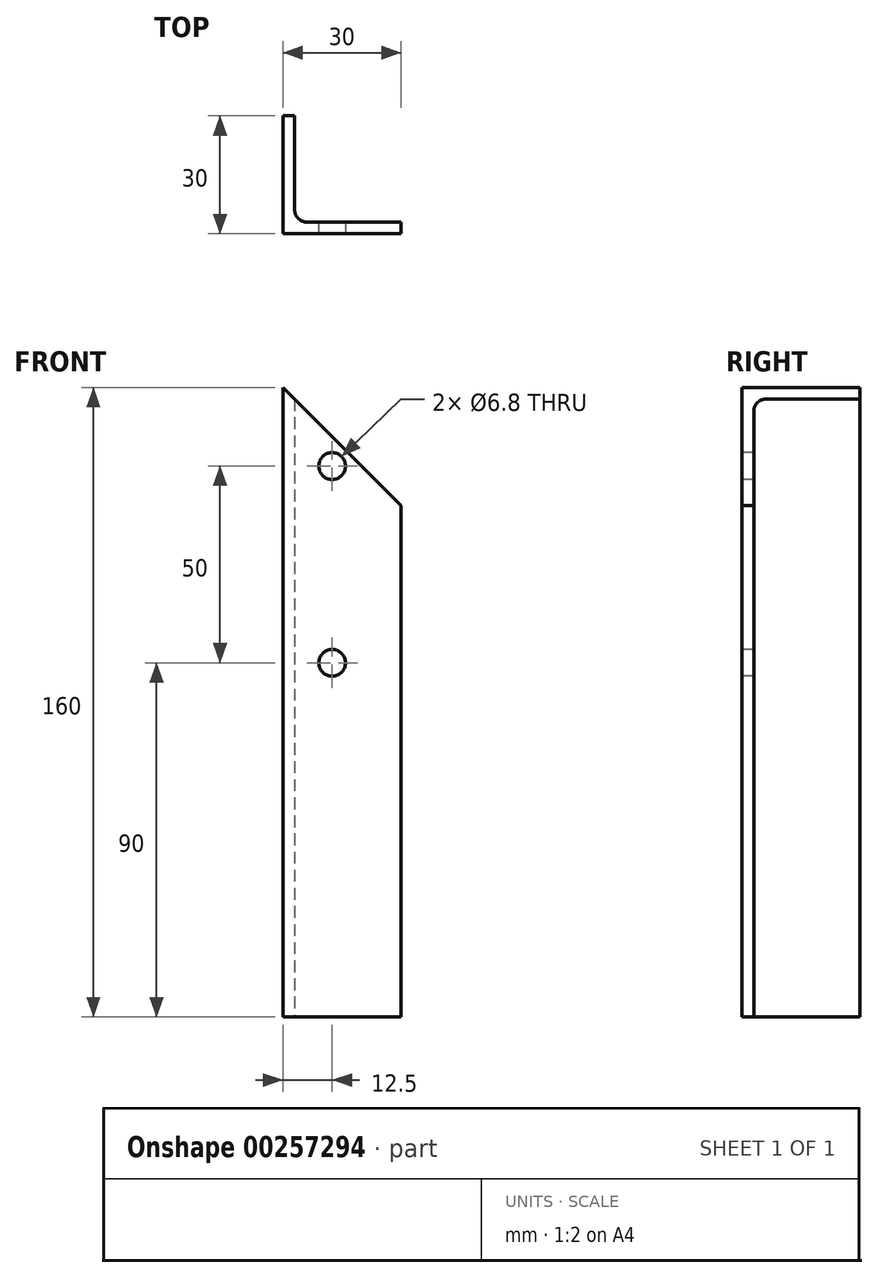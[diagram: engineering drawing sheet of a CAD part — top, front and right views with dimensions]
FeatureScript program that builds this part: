
annotation { "Feature Type Name" : "Feature", "Feature Type Description" : "" }
export const myFeature = defineFeature(function(context is Context, id is Id, definition is map)
    precondition{}
    {
        {
            var Q0;
            Q0=qCreatedBy(makeId("Top.planeOp"),FACE);
            var sketch = newSketch(context, id + "F0", { "sketchPlane" : qUnion([Q0])});
            skLineSegment(sketch, "E0", {"start": v(0, 30) * mm, "end": v(0, 0) * mm});
            skLineSegment(sketch, "E1", {"start": v(0, 0) * mm, "end": v(30, 0) * mm});
            skLineSegment(sketch, "E2", {"start": v(30, 0) * mm, "end": v(30, 3) * mm});
            skLineSegment(sketch, "E3", {"start": v(30, 3) * mm, "end": v(3, 3) * mm});
            skLineSegment(sketch, "E4", {"start": v(3, 3) * mm, "end": v(3, 30) * mm});
            skLineSegment(sketch, "E5", {"start": v(3, 30) * mm, "end": v(0, 30) * mm});
            skSolve(sketch);
        }
        {
            var Q0;
            Q0=makeQuery(id+"F0.imprint","IMPRINT",FACE,{"disambiguationData":[TD([[makeQuery(id+"F0.imprint","IMPRINT",EDGE,{"derivedFrom":sQuery(id+"F0.wireOp",EDGE,"E0")}),1.0]])]});
            extrude(context, id + "F1", {"entities" : qUnion([Q0]), "depth" : 160 * mm});
        }
        {
            var Q0;
            Q0=makeQuery(id+"F1.opExtrude","SWEPT_EDGE",EDGE,{"disambiguationData":[OSD([sQuery(id+"F0.wireOp",EDGE,"E3"),sQuery(id+"F0.wireOp",EDGE,"E4")])]});
            fillet(context, id + "F2", {"entities" : qUnion([Q0]), "radius" : 3 * mm, "tangentPropagation" : true, "allowEdgeOverflow" : false});
        }
        {
            var Q0;
            Q0=makeQuery(id+"F1.opExtrude","SWEPT_FACE",FACE,{"disambiguationData":[OSD([sQuery(id+"F0.wireOp",EDGE,"E1")])]});
            var sketch = newSketch(context, id + "F3", { "sketchPlane" : qUnion([Q0])});
            skLineSegment(sketch, "E6", {"start": v(-10, 170) * mm, "end": v(40, 120) * mm});
            skLineSegment(sketch, "E7", {"start": v(40, 120) * mm, "end": v(40, 170) * mm});
            skLineSegment(sketch, "E8", {"start": v(40, 170) * mm, "end": v(-10, 170) * mm});
            skPoint(sketch, "E9", {"position": v(0, 160) * mm});
            skPoint(sketch, "E10", {"position": v(30, 130) * mm});
            skSolve(sketch);
        }
        {
            var Q0;
            Q0 = qSketchRegion(id + "F3", true);
            extrude(context, id + "F4", {"entities" : qUnion([Q0]), "operationType" : NewBodyOperationType.REMOVE, "endBound" : BoundingType.THROUGH_ALL, "oppositeDirection" : true, "depth" : 25 * mm});
        }
        {
            var Q0;
            Q0=makeQuery(id+"F1.opExtrude","SWEPT_FACE",FACE,{"disambiguationData":[OSD([sQuery(id+"F0.wireOp",EDGE,"E1")])]});
            var sketch = newSketch(context, id + "F5", { "sketchPlane" : qUnion([Q0])});
            skPoint(sketch, "E11", {"position": v(12.5, 140) * mm});
            skPoint(sketch, "E12", {"position": v(12.5, 90) * mm});
            skSolve(sketch);
        }
        {
            var Q0;
            Q0=sQuery(id+"F5.wireOp",VERTEX,"E11");
            var Q1;
            Q1=sQuery(id+"F5.wireOp",VERTEX,"E12");
            var Q2;
            Q2=makeQuery(id+"F1.opExtrude","SWEPT_BODY",BODY,{"disambiguationData":[OSD([sQuery(id+"F0.wireOp",EDGE,"E0"),sQuery(id+"F0.wireOp",EDGE,"E1"),sQuery(id+"F0.wireOp",EDGE,"E2"),sQuery(id+"F0.wireOp",EDGE,"E3"),sQuery(id+"F0.wireOp",EDGE,"E4"),sQuery(id+"F0.wireOp",EDGE,"E5")])]});
            hole(context, id + "F6", {"style" : HoleStyle.SIMPLE, "endStyle" : HoleEndStyle.THROUGH, "standardTappedOrClearance" : lookupTablePath({ "standard" : "ISO", "fit" : "Normal", "engagement" : "75%", "pitch" : "1.25 mm", "size" : "M8", "type" : "Tapped" }), "standardBlindInLast" : lookupTablePath({ "fit" : "Standard", "standard" : "ISO", "engagement" : "75%", "pitch" : "1.25 mm", "size" : "M8", "type" : "Tapped" }), "holeDiameter" : 6.8 * mm, "showTappedDepth" : true, "tappedDepth" : 12 * mm, "tapClearance" : 3, "locations" : qUnion([Q0, Q1]), "scope" : qUnion([Q2]), "majorDiameter" : 8 * mm});
        }
    });
